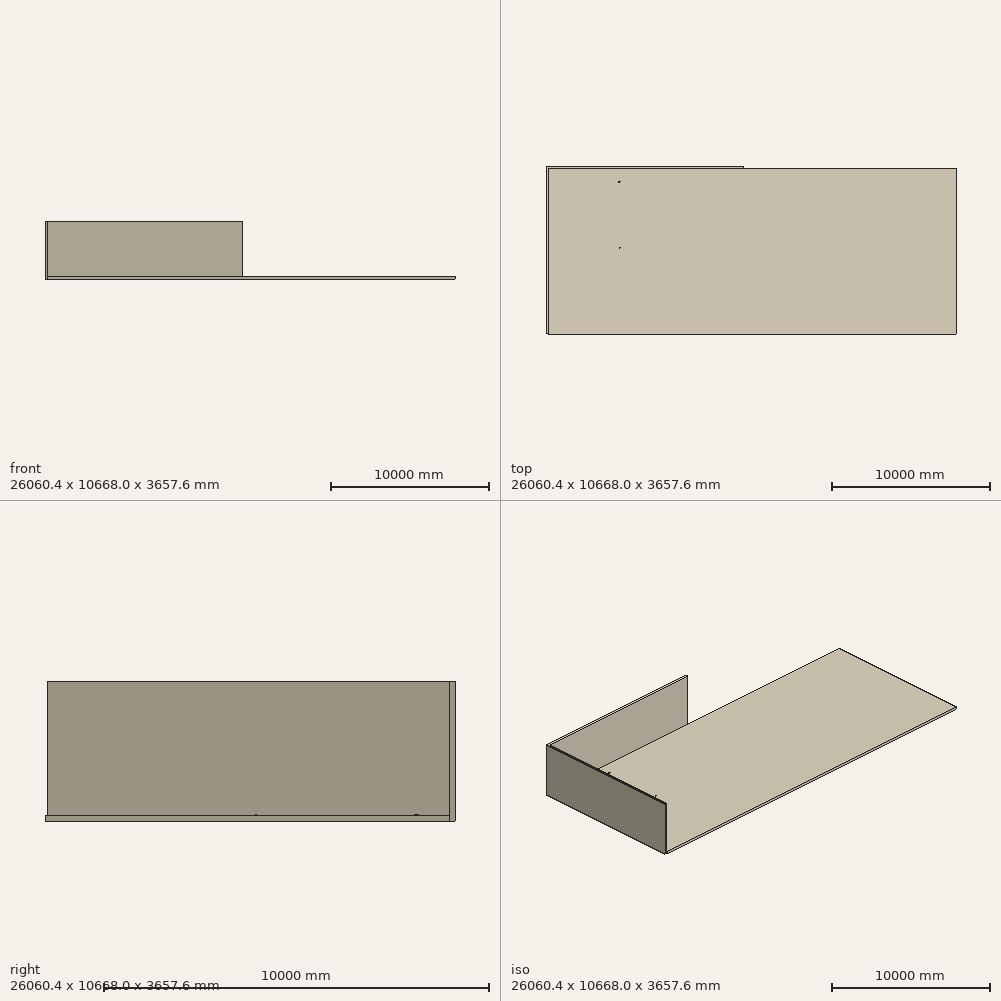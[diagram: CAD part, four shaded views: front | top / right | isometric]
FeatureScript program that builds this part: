
annotation { "Feature Type Name" : "Feature", "Feature Type Description" : "" }
export const myFeature = defineFeature(function(context is Context, id is Id, definition is map)
    precondition{}
    {
        {
            var Q0;
            Q0=qCreatedBy(makeId("Top.planeOp"),FACE);
            var sketch = newSketch(context, id + "F0", { "sketchPlane" : qUnion([Q0])});
            skLineSegment(sketch, "E0.bottom", {"start": v(12954, -5257.8) * mm, "end": v(-12954, -5257.8) * mm});
            skLineSegment(sketch, "E0.top", {"start": v(12954, 5257.8) * mm, "end": v(-12954, 5257.8) * mm});
            skLineSegment(sketch, "E0.left", {"start": v(12954, -5257.8) * mm, "end": v(12954, 5257.8) * mm});
            skLineSegment(sketch, "E0.right", {"start": v(-12954, -5257.8) * mm, "end": v(-12954, 5257.8) * mm});
            skPoint(sketch, "E0.middle", {"position": v(0, 0) * mm});
            skSolve(sketch);
        }
        {
            var Q0;
            Q0=makeQuery(id+"F0.imprint","IMPRINT",FACE,{"disambiguationData":[TD([[makeQuery(id+"F0.imprint","IMPRINT",EDGE,{"derivedFrom":sQuery(id+"F0.wireOp",EDGE,"E0.bottom")}),-1.0]])]});
            var sketch = newSketch(context, id + "F1", { "sketchPlane" : qUnion([Q0])});
            skLineSegment(sketch, "E1.bottom", {"start": v(-12954, 5257.8) * mm, "end": v(-13106.4, 5257.8) * mm});
            skLineSegment(sketch, "E1.top", {"start": v(-12954, -5205.2) * mm, "end": v(-13106.4, -5205.2) * mm});
            skLineSegment(sketch, "E1.left", {"start": v(-12954, 5257.8) * mm, "end": v(-12954, -5205.2) * mm});
            skLineSegment(sketch, "E1.right", {"start": v(-13106.4, 5257.8) * mm, "end": v(-13106.4, -5205.2) * mm});
            skLineSegment(sketch, "E2.bottom", {"start": v(-13106.4, 5257.8) * mm, "end": v(-609.6, 5257.8) * mm});
            skLineSegment(sketch, "E2.top", {"start": v(-13106.4, 5410.2) * mm, "end": v(-609.6, 5410.2) * mm});
            skLineSegment(sketch, "E2.left", {"start": v(-13106.4, 5257.8) * mm, "end": v(-13106.4, 5410.2) * mm});
            skLineSegment(sketch, "E2.right", {"start": v(-609.6, 5257.8) * mm, "end": v(-609.6, 5410.2) * mm});
            skSolve(sketch);
        }
        {
            var Q0;
            Q0 = qSketchRegion(id + "F1", true);
            extrude(context, id + "F2", {"entities" : qUnion([Q0]), "depth" : 3657.6 * mm});
        }
        {
            var Q0;
            Q0=makeQuery(id+"F0.imprint","IMPRINT",FACE,{"disambiguationData":[TD([[makeQuery(id+"F0.imprint","IMPRINT",EDGE,{"derivedFrom":sQuery(id+"F0.wireOp",EDGE,"E0.bottom")}),-1.0]])]});
            extrude(context, id + "F3", {"entities" : qUnion([Q0]), "operationType" : NewBodyOperationType.ADD, "depth" : 152.4 * mm});
        }
        {
            var Q0;
            Q0=makeQuery(id+"F3.opExtrude","CAP_FACE",FACE,{"disambiguationData":[OSD([sQuery(id+"F0.wireOp",EDGE,"E0.bottom"),sQuery(id+"F0.wireOp",EDGE,"E0.top"),sQuery(id+"F0.wireOp",EDGE,"E0.left"),sQuery(id+"F0.wireOp",EDGE,"E0.right")])],"isStart":false});
            var sketch = newSketch(context, id + "F4", { "sketchPlane" : qUnion([Q0])});
            skLineSegment(sketch, "E3", {"start": v(-8538.66, 4436.39) * mm, "end": v(-8458.2, 4343.4) * mm});
            skLineSegment(sketch, "E4", {"start": v(-8458.2, 4343.4) * mm, "end": v(-8400.03, 4436.39) * mm});
            skLineSegment(sketch, "E5", {"start": v(-8400.03, 4436.39) * mm, "end": v(-8538.66, 4436.39) * mm});
            skSolve(sketch);
        }
        {
            var Q0;
            Q0 = qSketchRegion(id + "F4", true);
            extrude(context, id + "F5", {"entities" : qUnion([Q0]), "operationType" : NewBodyOperationType.ADD, "depth" : 25.4 * mm});
        }
        {
            var Q0;
            Q0=makeQuery(id+"F3.opExtrude","CAP_FACE",FACE,{"disambiguationData":[OSD([sQuery(id+"F0.wireOp",EDGE,"E0.bottom"),sQuery(id+"F0.wireOp",EDGE,"E0.top"),sQuery(id+"F0.wireOp",EDGE,"E0.left"),sQuery(id+"F0.wireOp",EDGE,"E0.right")])],"isStart":false});
            var sketch = newSketch(context, id + "F6", { "sketchPlane" : qUnion([Q0])});
            skLineSegment(sketch, "E6", {"start": v(-8458.2, 203.2) * mm, "end": v(-8497.4, 245.28) * mm});
            skLineSegment(sketch, "E7", {"start": v(-8497.4, 245.28) * mm, "end": v(-8420.78, 245.28) * mm});
            skLineSegment(sketch, "E8", {"start": v(-8420.78, 245.28) * mm, "end": v(-8458.2, 203.2) * mm});
            skSolve(sketch);
        }
        {
            var Q0;
            Q0 = qSketchRegion(id + "F6", true);
            extrude(context, id + "F7", {"entities" : qUnion([Q0]), "operationType" : NewBodyOperationType.ADD, "depth" : 25.4 * mm});
        }
    });
